# Revit family: Diverter-American_Standard-Portsmouth-T42073X_Series.rfaxxx
name_source: partatom
category: Plumbing Fixtures
units: mm (PartAtom-declared; Revit-internal decimal feet)

## family parameters
Cut with Voids When Loaded = No
Host = Face
OmniClass Number = 23.65.55.14
OmniClass Title = Valves for Liquid Services
Part Type = Normal
Room Calculation Point = No
Round Connector Dimension = Use Diameter
Shared = Yes

## types (2) — shared parameters
ADA Compliant = Yes
Assembly Code = D2020300
C = 1/2"
CW Connection = Yes
CWFU = 3
Cold Water Connection Diameter = 0"
Compliance Certifications = ASSE 1016, ASME A112.18.1 & CSA B125.1
Default Elevation = 48"
HW Connection = Yes
HWFU = 3
Height = 9 1/2"
Hot Water Connection Diameter = 0"
InletOutlet Radius = 1/4"
Installation Type = Wall Mounted
Manufacturer = American Standard
Maximum Temperature = 104-109°F
Price = Prices may vary. Please consult Manufacturer Representative for most up-to-date price list.
Product Documentation Link = https://americanstandard.box.com
R510 = 0"
R510 Rough Valve Body 1/2" NPT Inlets/Outlets (Sold Separately) = No
R530 = 0"
R530 Rough Valve Body 3/4" NPT Inlets/Outlets (Sold Separately) = No
Tempered Water Connection = Yes
Tempered Water Connection Diameter = 0"
Valve Rough-In = No
Vent Connection = No
WFU = 4
Waste Connection = No
Width = 6"

## per-type parameters (varying)
| type | Cross Handle | Description | Finish | Lever Handle | Material | Product Page URL | URL |
| T420730.002 | No | Portsmouth Single Handle Thermostatic Shower Valve Trim Kit with Lever Handle | Cast Brass-American Standard-002-Polished Chrome | Yes | Cast Brass-American Standard-002-Polished Chrome | https://www.americanstandard.ca | https://www.americanstandard.ca |
| T420732.224 | Yes | Portsmouth Single Handle Thermostatic Shower Valve Trim Kit with Cross Handle | Cast Brass-American Standard-224-Oil Rubbed Bronze | No | Cast Brass-American Standard-224-Oil Rubbed Bronze | https://www.americanstandard-us.com | https://www.americanstandard-us.com |

note: column(s) folded — value = type name in every type: Model

## geometry (parser evidence)
native form markers: Sweep x2
no freeform markers — native parametric forms only
